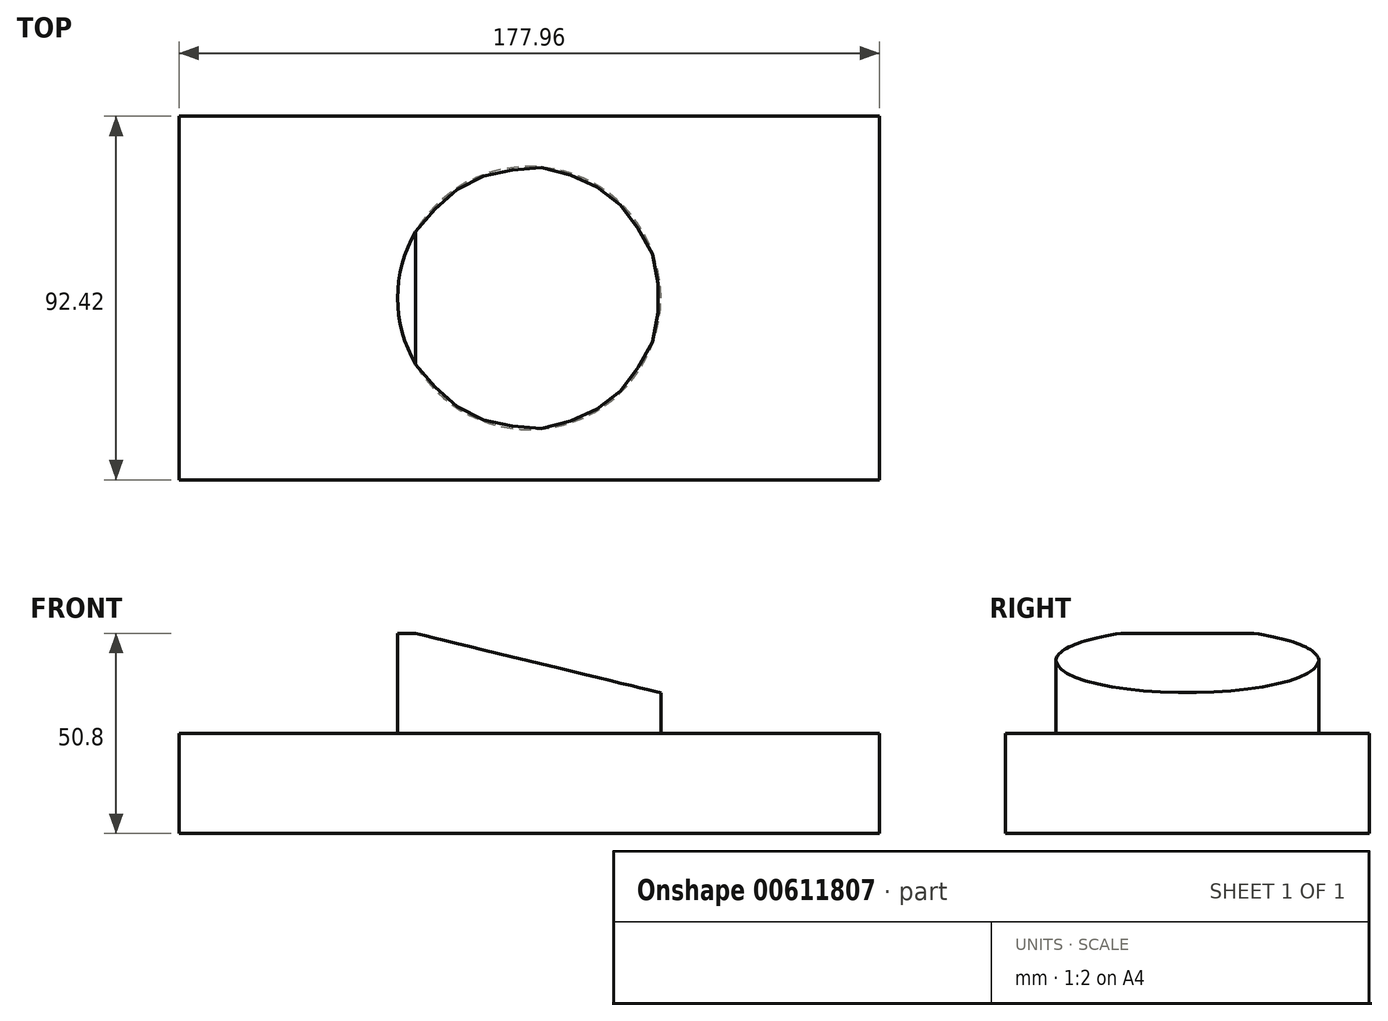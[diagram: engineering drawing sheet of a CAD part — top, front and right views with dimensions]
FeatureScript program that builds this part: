
annotation { "Feature Type Name" : "Feature", "Feature Type Description" : "" }
export const myFeature = defineFeature(function(context is Context, id is Id, definition is map)
    precondition{}
    {
        {
            var Q0;
            Q0=qCreatedBy(makeId("Top.planeOp"),FACE);
            var sketch = newSketch(context, id + "F0", { "sketchPlane" : qUnion([Q0])});
            skLineSegment(sketch, "E0.bottom", {"start": v(-88.98, 46.2) * mm, "end": v(88.98, 46.2) * mm});
            skLineSegment(sketch, "E0.top", {"start": v(-88.98, -46.2) * mm, "end": v(88.98, -46.2) * mm});
            skLineSegment(sketch, "E0.left", {"start": v(-88.98, 46.2) * mm, "end": v(-88.98, -46.2) * mm});
            skLineSegment(sketch, "E0.right", {"start": v(88.98, 46.2) * mm, "end": v(88.98, -46.2) * mm});
            skPoint(sketch, "E0.middle", {"position": v(0, 0) * mm});
            skCircle(sketch, "E1", {"center": v(0, 0) * mm, "radius": 33.42 * mm});
            skSolve(sketch);
        }
        {
            var Q0;
            Q0=makeQuery(id+"F0.imprint","IMPRINT",FACE,{"disambiguationData":[TD([[makeQuery(id+"F0.imprint","IMPRINT",EDGE,{"derivedFrom":sQuery(id+"F0.wireOp",EDGE,"E0.bottom")}),-1.0]])]});
            var Q1;
            Q1=makeQuery(id+"F0.imprint","IMPRINT",FACE,{"disambiguationData":[TD([[makeQuery(id+"F0.imprint","IMPRINT",EDGE,{"derivedFrom":sQuery(id+"F0.wireOp",EDGE,"E1")}),1.0]])]});
            extrude(context, id + "F1", {"entities" : qUnion([Q0, Q1]), "depth" : 25.4 * mm, "offsetDistance" : 25.4 * mm});
        }
        {
            var Q0;
            Q0=makeQuery(id+"F0.imprint","IMPRINT",FACE,{"disambiguationData":[TD([[makeQuery(id+"F0.imprint","IMPRINT",EDGE,{"derivedFrom":sQuery(id+"F0.wireOp",EDGE,"E1")}),1.0]])]});
            extrude(context, id + "F2", {"entities" : qUnion([Q0]), "operationType" : NewBodyOperationType.ADD, "depth" : 50.8 * mm, "offsetDistance" : 25.4 * mm});
        }
        {
            var Q0;
            Q0=qCreatedBy(makeId("Front.planeOp"),FACE);
            var sketch = newSketch(context, id + "F3", { "sketchPlane" : qUnion([Q0])});
            skLineSegment(sketch, "E2", {"start": v(-43.01, 54.24) * mm, "end": v(44.76, 32.95) * mm});
            skLineSegment(sketch, "E3", {"start": v(44.76, 32.95) * mm, "end": v(44.76, 56.28) * mm});
            skLineSegment(sketch, "E4", {"start": v(44.76, 56.28) * mm, "end": v(-43.01, 54.24) * mm});
            skSolve(sketch);
        }
        {
            var Q0;
            Q0 = qSketchRegion(id + "F3", true);
            extrude(context, id + "F4", {"entities" : qUnion([Q0]), "operationType" : NewBodyOperationType.REMOVE, "endBound" : BoundingType.SYMMETRIC, "oppositeDirection" : true, "depth" : 76.2 * mm, "offsetDistance" : 25.4 * mm});
        }
    });
